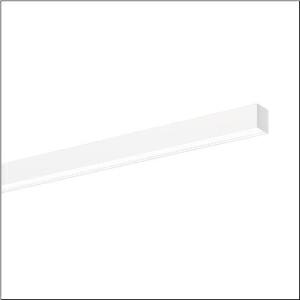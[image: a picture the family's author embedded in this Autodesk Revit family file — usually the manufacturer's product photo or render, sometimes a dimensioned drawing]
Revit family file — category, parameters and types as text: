
# Revit family: silica_21_51mx23db45wb
name_source: partatom
category: Lighting Fixtures
units: mm (PartAtom-declared; Revit-internal decimal feet)

## family parameters
Cut with Voids When Loaded = No
Host = Face
Light Source = No
Part Type = Normal
Room Calculation Point = No
Round Connector Dimension = Use Diameter
Shared = No

## types (1)
- --- (1 x LED, 4100 lm, 28.1 W, 4000K)
    Apparent Load = 28 VA
    CIE Flux Codes = 78 96 99 100 100
    Color Rendering = 80
    Color Temperature = 4000K
    Default Elevation = 1800 mm
    Description = Silica 21, office luminaire, primary optical cover: prismatic diffuser, of PMMA, CAT 2 (L<= 3000cd/m²), light emission: direct distribution, primary light characteristic: symmetric, installation type: surface-mounted, LED, rated luminous flux: 4.100lm, luminous efficacy: 146lm/W, light colour: 840, colour temperature: 4000K, control gear: DALI 2, with terminal, 3+2-pole, max. 2.5mm², mains connection: 220..240V, AC, 50/60Hz, rated input power: 28.1W, luminaire housing, of aluminium, traffic white (RAL 9016), length: 1.504mm, width: 53mm, height: 53mm, protection rating (complete): IP20, insulation class (complete): insulation class I (protective earthing), certification: CE, permissible operating ambient temperature: 0..+35°C, standard: EN 50419, packaging unit: 1 piece
    Height = 53 mm
    Lamp = 1 x LED
    Lamp Light Flux = 4100 lm
    Lamp Power = 28.1 W
    Lamp count = 1
    Length = 1504 mm
    Luminous efficacy = 146 lm/W
    Manufacturer = Siteco
    ModVariant = No
    Model = 51MX23DB45WB
    Mounting Place = Ceiling
    Mounting Type = Surface mounted
    Number of Poles = 1
    OnlyDefault = Yes
    Power Factor = 1
    Product Name = Silica 21
    Product group = office luminaire | ceiling mounted
    ProductGroupID = 301
    Protection Class = Protection class I
    Protection Degree = IP 20
    RLX_Detail_Level = 1
    RLX_Emergency_Light_Flux = 0 lm
    RLX_Emergency_Type = 0
    RLX_Emergency_Type_DB = No
    RlxData = <blob elided: 18881 chars, md5=0a156827>
    Socket = socket
    Standby Power = 0 W
    System Light Flux = 4100 lm
    System Power = 28 W
    Type Comments = factory setting: luminous flux: 100 % | dim-lin: 254 | 323 mA
    Type Image = l_1335877.jpg
    URL = http://relux.com
    VarID = @adj_121313
    Voltage = 0 V
    Weight = 0.00 kg
    Width = 53 mm

## geometry (parser evidence)
native form markers: Blend x4, Sweep x13
no freeform markers — native parametric forms only
